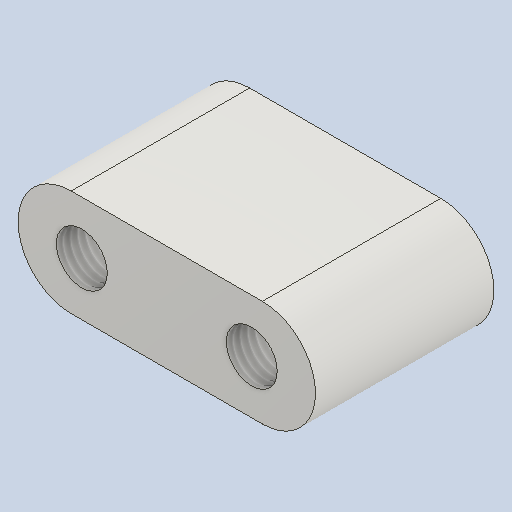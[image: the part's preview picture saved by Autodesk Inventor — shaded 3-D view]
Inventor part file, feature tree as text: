
AUTODESK INVENTOR PART (.ipt)
format: ipt  version: 2024 (Build 280153000, 153)  size: 247,296 bytes
history: native  units: mm
features: extrude x2, other x2, thread x2, sketch x2
ambient origin geometry x8: Origin, YZ Plane, XZ Plane, XY Plane, X Axis, Y Axis, Z Axis, Center Point
bodies: Solid1 (feature_tree)
feature tree (8):
  extrude  "Extrusion1"  Depth=25.0mm
  other  "Full Round Fillet1"
  other  "Full Round Fillet2"
  extrude  "Extrusion2"  Depth=12.5mm
  thread  "Thread1"  [1 undecoded]
  thread  "Thread2"  [1 undecoded]
  sketch  "Sketch1"  dims[d0=70.0mm d1=25.0mm]
  sketch  "Sketch2"  dims[d2=35.0mm d3=12.5mm d4=42.0mm d5=0.0mm d6=12.0mm d7=12.0mm d8=40.0mm d9=20.0mm d10=42.0mm d11=0.0mm d12=42.0mm d13=0.0mm d14=42.0mm d15=0.0mm]
note: 2 required parameter values undecoded (feature->parameter linkage not recoverable at this tier; creation-order binding heuristic only, values carry confidence <= 0.55)
